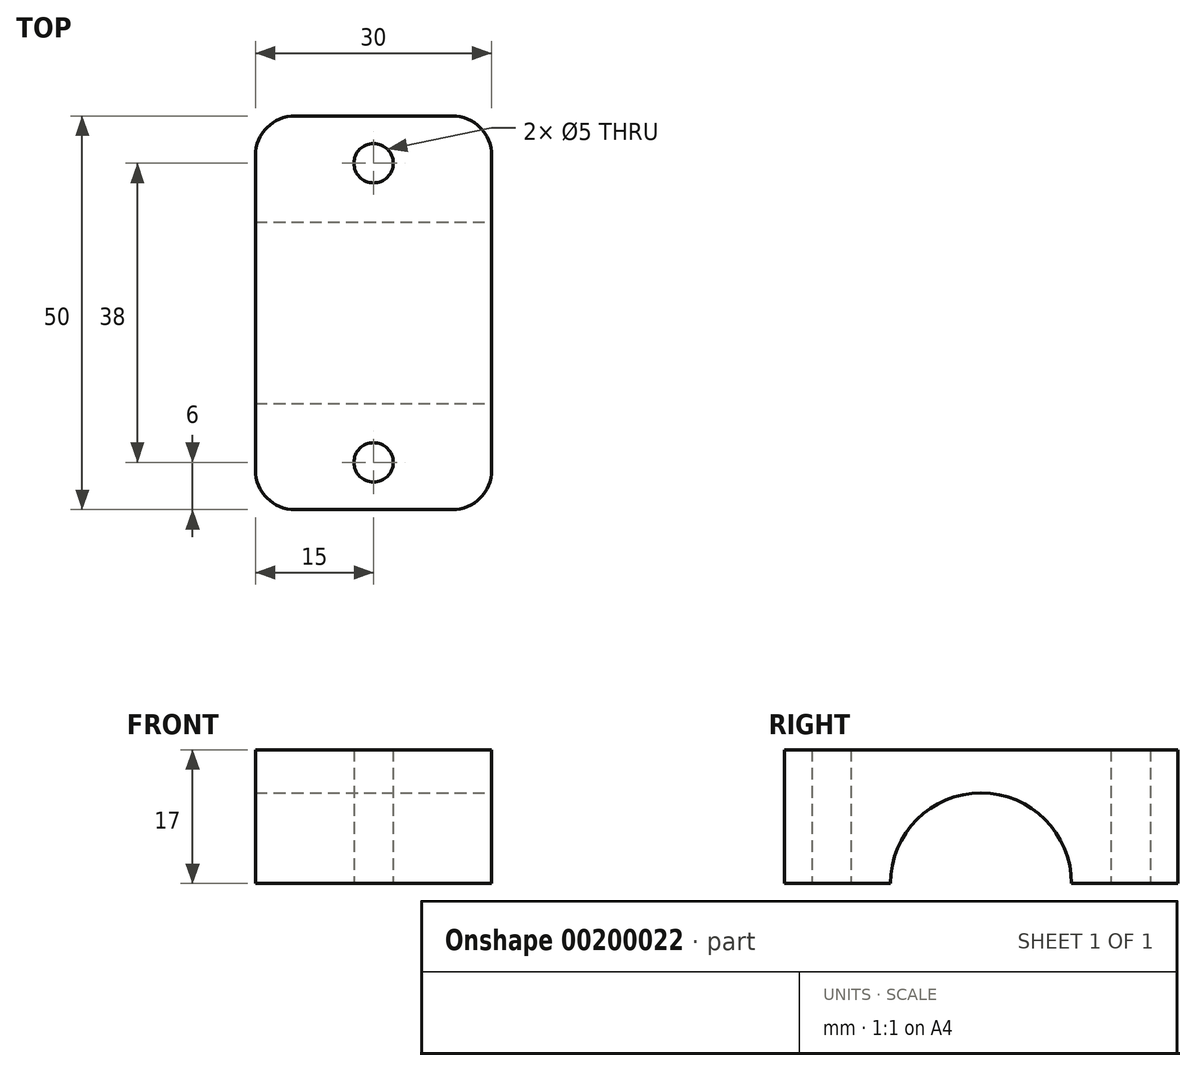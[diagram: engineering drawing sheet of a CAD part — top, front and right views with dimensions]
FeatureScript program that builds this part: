
annotation { "Feature Type Name" : "Feature", "Feature Type Description" : "" }
export const myFeature = defineFeature(function(context is Context, id is Id, definition is map)
    precondition{}
    {
        {
            var Q0;
            Q0=qCreatedBy(makeId("Top.planeOp"),FACE);
            var sketch = newSketch(context, id + "F0", { "sketchPlane" : qUnion([Q0])});
            skPoint(sketch, "E0", {"position": v(-15, 0) * mm});
            skPoint(sketch, "E1", {"position": v(15, 0) * mm});
            skPoint(sketch, "E2", {"position": v(0, 25) * mm});
            skPoint(sketch, "E3", {"position": v(0, -25) * mm});
            skPoint(sketch, "E4", {"position": v(0, 0) * mm});
            skPoint(sketch, "E5", {"position": v(0, 19) * mm});
            skPoint(sketch, "E6", {"position": v(0, -19) * mm});
            skLineSegment(sketch, "E7.bottom", {"start": v(-15, -25) * mm, "end": v(15, -25) * mm});
            skLineSegment(sketch, "E7.top", {"start": v(-15, 25) * mm, "end": v(15, 25) * mm});
            skLineSegment(sketch, "E7.left", {"start": v(-15, -25) * mm, "end": v(-15, 25) * mm});
            skLineSegment(sketch, "E7.right", {"start": v(15, -25) * mm, "end": v(15, 25) * mm});
            skLineSegment(sketch, "E8", {"start": v(-15, 0) * mm, "end": v(15, 0) * mm});
            skSolve(sketch);
        }
        {
            var Q0;
            {var subQ0=sQuery(id+"F0.wireOp",EDGE,"E7.top");Q0=makeQuery(id+"F0.imprint","IMPRINT",FACE,{"disambiguationData":[TD([[makeQuery(id+"F0.imprint","IMPRINT",EDGE,{"derivedFrom":subQ0}),-1.0]])]});}
            var Q1;
            {var subQ0=sQuery(id+"F0.wireOp",EDGE,"E7.bottom");Q1=makeQuery(id+"F0.imprint","IMPRINT",FACE,{"disambiguationData":[TD([[makeQuery(id+"F0.imprint","IMPRINT",EDGE,{"derivedFrom":subQ0}),1.0]])]});}
            extrude(context, id + "F1", {"entities" : qUnion([Q0, Q1]), "depth" : 17 * mm});
        }
        {
            var Q0;
            Q0=sQuery(id+"F0.wireOp",VERTEX,"E5");
            var Q1;
            Q1=sQuery(id+"F0.wireOp",VERTEX,"E6");
            var Q2;
            Q2=makeQuery(id+"F1.opExtrude","SWEPT_BODY",BODY,{"disambiguationData":[OSD([sQuery(id+"F0.wireOp",EDGE,"E7.bottom"),sQuery(id+"F0.wireOp",EDGE,"E7.top"),sQuery(id+"F0.wireOp",EDGE,"E7.left"),sQuery(id+"F0.wireOp",EDGE,"E7.right")])]});
            hole(context, id + "F2", {"style" : HoleStyle.SIMPLE, "endStyle" : HoleEndStyle.THROUGH, "oppositeDirection" : true, "holeDiameter" : 5 * mm, "locations" : qUnion([Q0, Q1]), "scope" : qUnion([Q2]), "isTappedThrough" : true});
        }
        {
            var Q0;
            Q0=makeQuery(id+"F1.opExtrude","SWEPT_FACE",FACE,{"disambiguationData":[OSD([sQuery(id+"F0.wireOp",EDGE,"E7.right")])]});
            var sketch = newSketch(context, id + "F3", { "sketchPlane" : qUnion([Q0])});
            skCircle(sketch, "E9", {"center": v(0, 0) * mm, "radius": 11.5 * mm});
            skSolve(sketch);
        }
        {
            var Q0;
            {var subQ0=sQuery(id+"F3.wireOp",EDGE,"E9");var subQ1=makeQuery(id+"F1.opExtrude","CAP_EDGE",EDGE,{"disambiguationData":[OSD([sQuery(id+"F0.wireOp",EDGE,"E7.right")])],"isStart":true});var subQ2=makeQuery(id+"F3.imprint","INTERSECT",VERTEX,{"disambiguationData":[OD(0.0)],"derivedFrom":[subQ1,subQ0]});Q0=makeQuery(id+"F3.imprint","IMPRINT",FACE,{"disambiguationData":[TD([[makeQuery(id+"F3.imprint","IMPRINT",EDGE,{"disambiguationData":[TD([[subQ2,1.0]])],"derivedFrom":subQ0}),1.0]])]});}
            var Q1;
            {var subQ0=sQuery(id+"F3.wireOp",EDGE,"E9");var subQ1=makeQuery(id+"F1.opExtrude","CAP_EDGE",EDGE,{"disambiguationData":[OSD([sQuery(id+"F0.wireOp",EDGE,"E7.right")])],"isStart":true});var subQ2=makeQuery(id+"F3.imprint","INTERSECT",VERTEX,{"disambiguationData":[OD(0.0)],"derivedFrom":[subQ1,subQ0]});Q1=makeQuery(id+"F3.imprint","IMPRINT",FACE,{"disambiguationData":[TD([[makeQuery(id+"F3.imprint","IMPRINT",EDGE,{"disambiguationData":[TD([[subQ2,-1.0]])],"derivedFrom":subQ0}),1.0]])]});}
            extrude(context, id + "F4", {"entities" : qUnion([Q0, Q1]), "operationType" : NewBodyOperationType.REMOVE, "oppositeDirection" : true, "depth" : 50 * mm});
        }
        {
            var Q0;
            Q0=makeQuery(id+"F1.opExtrude","SWEPT_EDGE",EDGE,{"disambiguationData":[OSD([sQuery(id+"F0.wireOp",EDGE,"E7.bottom"),sQuery(id+"F0.wireOp",EDGE,"E7.right")])]});
            var Q1;
            Q1=makeQuery(id+"F1.opExtrude","SWEPT_EDGE",EDGE,{"disambiguationData":[OSD([sQuery(id+"F0.wireOp",EDGE,"E7.bottom"),sQuery(id+"F0.wireOp",EDGE,"E7.left")])]});
            var Q2;
            Q2=makeQuery(id+"F1.opExtrude","SWEPT_EDGE",EDGE,{"disambiguationData":[OSD([sQuery(id+"F0.wireOp",EDGE,"E7.top"),sQuery(id+"F0.wireOp",EDGE,"E7.right")])]});
            var Q3;
            Q3=makeQuery(id+"F1.opExtrude","SWEPT_EDGE",EDGE,{"disambiguationData":[OSD([sQuery(id+"F0.wireOp",EDGE,"E7.top"),sQuery(id+"F0.wireOp",EDGE,"E7.left")])]});
            fillet(context, id + "F5", {"entities" : qUnion([Q0, Q1, Q2, Q3]), "radius" : 5 * mm, "tangentPropagation" : true, "allowEdgeOverflow" : false});
        }
    });
